# Revit family: Pilona Flexible HFLEX LED
name_source: partatom
category: Furniture
units: mm (PartAtom-declared; Revit-internal decimal feet)

## family parameters
Always vertical = Yes
Cut with Voids When Loaded = No
OmniClass Number = 23.40.20.00
OmniClass Title = General Furniture and Specialties
Room Calculation Point = No
Shared = No
Work Plane-Based = No

## types (1)
- Pilona Flexible Luminosa Con LED-HFLEXLED-1040mm
    A = 0.1 m
    Default Elevation = 0 m
    Description = Pilona luminosa con LED, fabricada en poliuretano flexible en color negro (opcional en rojo, verde, amarillo o azul), resistente a los rayos UV, con
una banda reflectante
    Fabricante = BENITO URBAN SL
    Ficha_Tecnica = https://www.benito.com
    H = 1.04 m
    H1 = 0.19 m
    Material = Poliuretano flexible
    Material LED = LED verde
    Referencia = HFLEXLED
    Type Comments = Se fabrica en variante fija o móvil con bases de poliuretano o de acero inoxidable. También en versión con peana para instalación atornillada.
Supera una flexión de 1500 ciclos a 45º y 50 ciclos a 90º, sin daños. Clasificación “E” de comportamiento al fuego, según norma UNE-EN
13501-1:2007+A1:2010.
Resistente a -50º según norma UNE ISO 812.
Anclaje recomendado: Mediante encastamiento.
    URL_Producto = https://www.benito.com

## geometry (parser evidence)
native form markers: Blend x6, Sweep x3
no freeform markers — native parametric forms only
